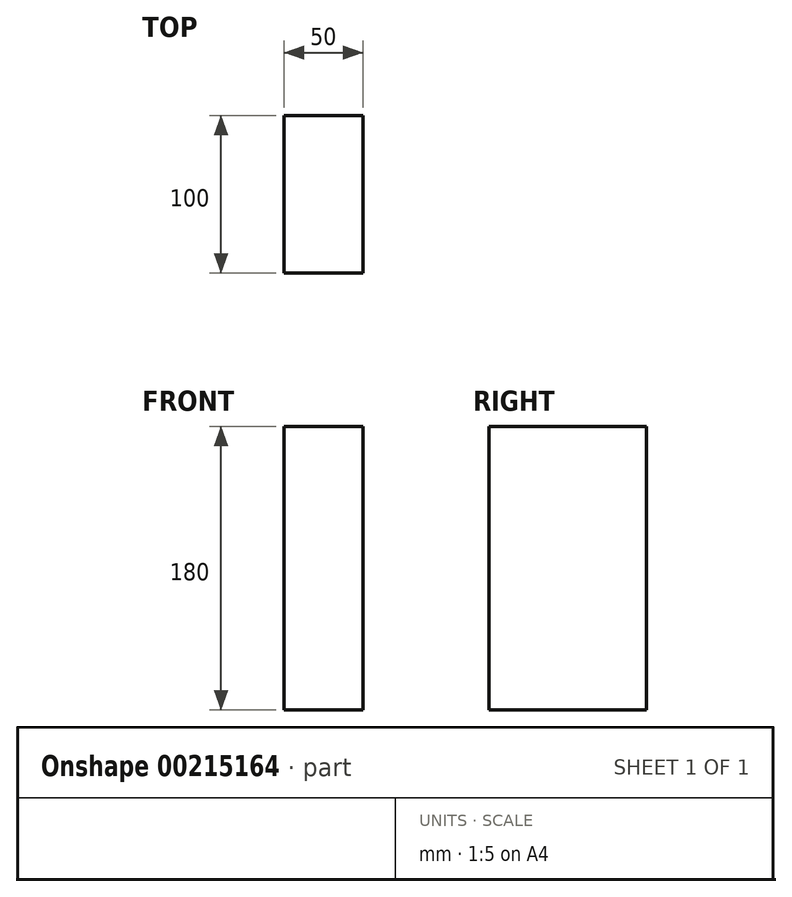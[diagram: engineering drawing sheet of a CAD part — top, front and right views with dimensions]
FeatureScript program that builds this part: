
annotation { "Feature Type Name" : "Feature", "Feature Type Description" : "" }
export const myFeature = defineFeature(function(context is Context, id is Id, definition is map)
    precondition{}
    {
        {
            var Q0;
            Q0=qCreatedBy(makeId("Right.planeOp"),FACE);
            var sketch = newSketch(context, id + "F0", { "sketchPlane" : qUnion([Q0])});
            skLineSegment(sketch, "E0.bottom", {"start": v(0, 90) * mm, "end": v(100, 90) * mm});
            skLineSegment(sketch, "E0.top", {"start": v(0, -90) * mm, "end": v(100, -90) * mm});
            skLineSegment(sketch, "E0.left", {"start": v(0, 90) * mm, "end": v(0, -90) * mm});
            skLineSegment(sketch, "E0.right", {"start": v(100, 90) * mm, "end": v(100, -90) * mm});
            skSolve(sketch);
        }
        {
            var Q0;
            Q0 = qSketchRegion(id + "F0", true);
            extrude(context, id + "F1", {"entities" : qUnion([Q0]), "depth" : 50 * mm});
        }
        {
            var Q0;
            Q0=qCreatedBy(makeId("Right.planeOp"),FACE);
            cPlane(context, id + "F2", {"entities" : qUnion([Q0]), "cplaneType" : CPlaneType.OFFSET, "offset" : 10 * mm, "width" : 150 * mm, "height" : 150 * mm});
        }
    });
